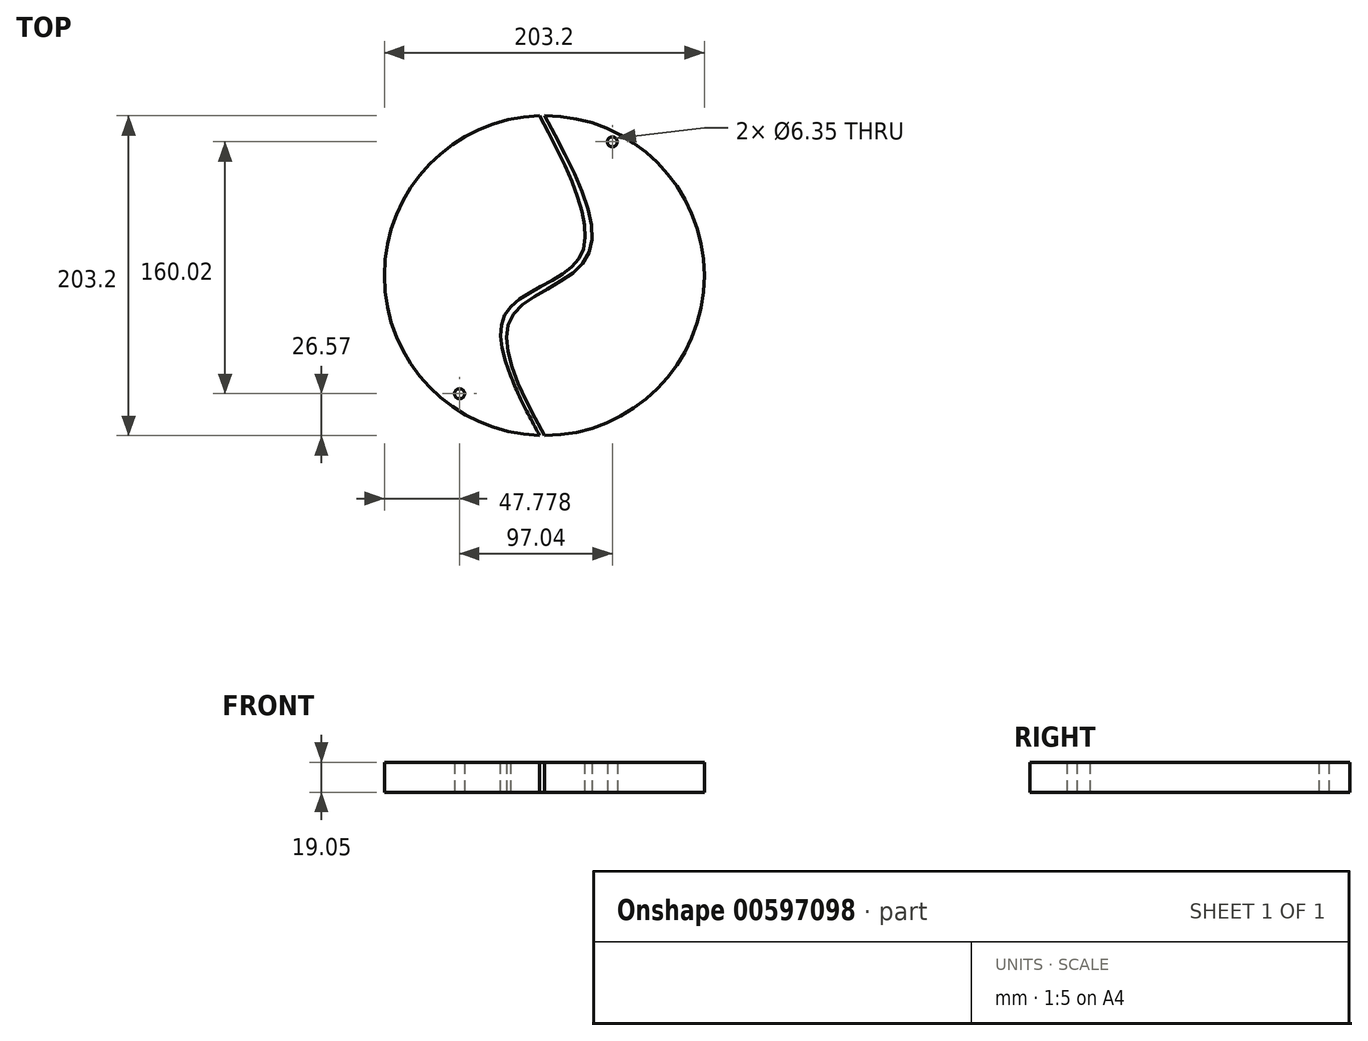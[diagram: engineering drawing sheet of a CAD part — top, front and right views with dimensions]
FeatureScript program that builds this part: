
annotation { "Feature Type Name" : "Feature", "Feature Type Description" : "" }
export const myFeature = defineFeature(function(context is Context, id is Id, definition is map)
    precondition{}
    {
        {
            var Q0;
            Q0=qCreatedBy(makeId("Top.planeOp"),FACE);
            var sketch = newSketch(context, id + "F0", { "sketchPlane" : qUnion([Q0])});
            skCircle(sketch, "E0", {"center": v(0, 0) * mm, "radius": 101.6 * mm});
            skCircle(sketch, "E1", {"center": v(43.22, 85) * mm, "radius": 3.18 * mm});
            skCircle(sketch, "E2", {"center": v(-53.82, -75.03) * mm, "radius": 3.18 * mm});
            skFitSpline(sketch, "E3", {"points": [v(0, 101.6) * mm, v(26.83, 11.09) * mm, v(-20.73, -26.19) * mm, v(0, -101.6) * mm], "startDerivative": vector(156.5, -286.93) * mm, "endDerivative": vector(138.84, -259.56) * mm});
            skFitSpline(sketch, "E4.0", {"points": [v(-2.23, 100.38) * mm, v(1.03, 94.4) * mm, v(7.54, 82.47) * mm, v(16.37, 65.09) * mm, v(22.19, 51.43) * mm, v(25.48, 41.27) * mm, v(27.16, 34.1) * mm, v(27.95, 27.48) * mm, v(27.8, 22.46) * mm, v(27.18, 18.78) * mm, v(26.44, 16.19) * mm, v(25.44, 13.76) * mm, v(24.16, 11.49) * mm, v(22.56, 9.33) * mm, v(20.04, 6.56) * mm, v(16.23, 3.31) * mm, v(10.85, -0.33) * mm, v(4.96, -3.8) * mm, v(-1.15, -7.23) * mm, v(-7.2, -10.74) * mm, v(-12.93, -14.48) * mm, v(-17.2, -17.94) * mm, v(-20.15, -21.02) * mm, v(-22.1, -23.5) * mm, v(-23.72, -26.2) * mm, v(-24.96, -29.07) * mm, v(-25.85, -32.06) * mm, v(-26.6, -36.2) * mm, v(-26.74, -41.64) * mm, v(-25.86, -48.5) * mm, v(-24.09, -55.65) * mm, v(-21.57, -63.08) * mm, v(-17.38, -73.3) * mm, v(-10.93, -86.55) * mm, v(-5.13, -97.4) * mm, v(-2.24, -102.8) * mm]});
            skFitSpline(sketch, "E5", {"points": [v(-2.96, 101.56) * mm, v(22.22, 11.09) * mm, v(-24.32, -23.52) * mm, v(-2.9, -101.56) * mm], "startDerivative": vector(150.98, -289.84) * mm, "endDerivative": vector(140.67, -267.02) * mm});
            skSolve(sketch);
        }
        {
            var Q0;
            Q0=makeQuery(id+"F0.imprint","IMPRINT",FACE,{"disambiguationData":[TD([[makeQuery(id+"F0.imprint","IMPRINT",EDGE,{"derivedFrom":sQuery(id+"F0.wireOp",EDGE,"E2")}),-1.0]])]});
            var Q1;
            Q1=makeQuery(id+"F0.imprint","IMPRINT",FACE,{"disambiguationData":[TD([[makeQuery(id+"F0.imprint","IMPRINT",EDGE,{"derivedFrom":sQuery(id+"F0.wireOp",EDGE,"E1")}),-1.0]])]});
            extrude(context, id + "F1", {"entities" : qUnion([Q0, Q1]), "depth" : 19.05 * mm, "offsetDistance" : 25.4 * mm});
        }
    });
